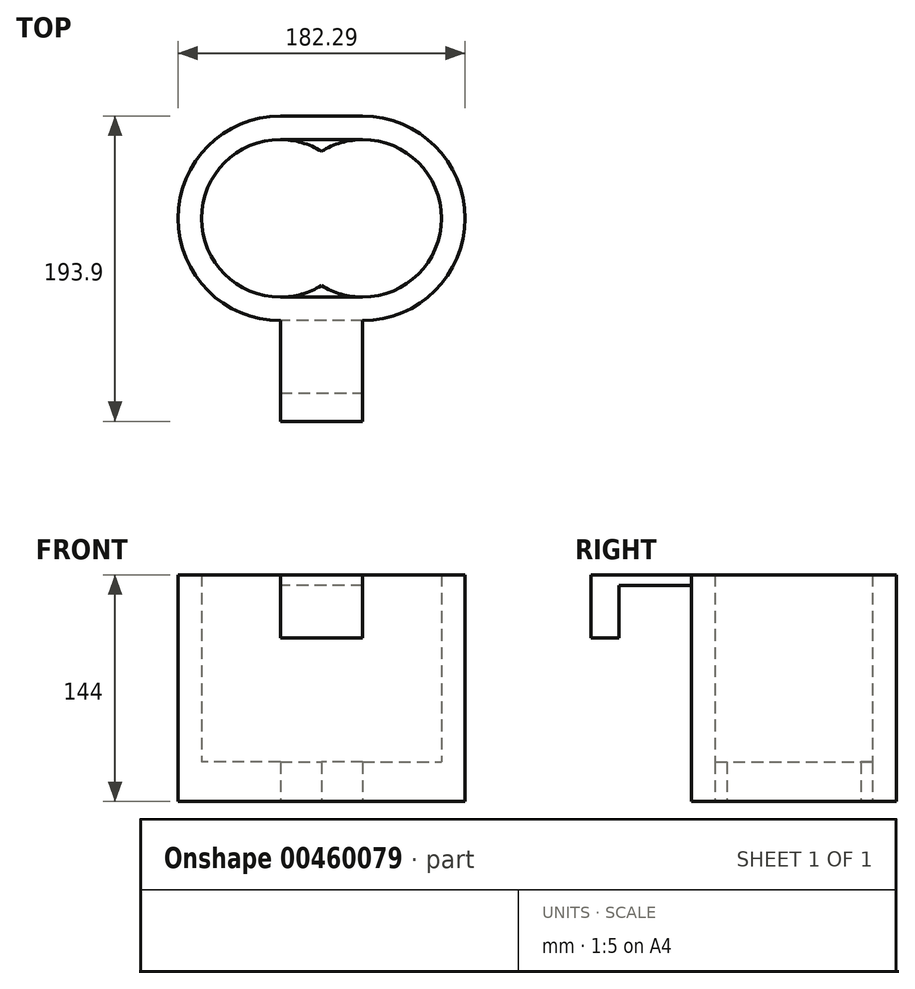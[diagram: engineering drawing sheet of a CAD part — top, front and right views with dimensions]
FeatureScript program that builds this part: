
annotation { "Feature Type Name" : "Feature", "Feature Type Description" : "" }
export const myFeature = defineFeature(function(context is Context, id is Id, definition is map)
    precondition{}
    {
        {
            var Q0;
            Q0=qCreatedBy(makeId("Top.planeOp"),FACE);
            var sketch = newSketch(context, id + "F0", { "sketchPlane" : qUnion([Q0])});
            skCircle(sketch, "E0", {"center": v(-48.66, 0) * mm, "radius": 65 * mm});
            skCircle(sketch, "E1", {"center": v(3.63, 0) * mm, "radius": 65 * mm});
            skLineSegment(sketch, "E2", {"start": v(3.63, -65) * mm, "end": v(-48.66, -65) * mm});
            skLineSegment(sketch, "E3", {"start": v(-48.66, 65) * mm, "end": v(3.63, 65) * mm});
            skCircle(sketch, "E4", {"center": v(-48.66, 0) * mm, "radius": 50 * mm});
            skCircle(sketch, "E5", {"center": v(3.63, 0) * mm, "radius": 50 * mm});
            skLineSegment(sketch, "E6", {"start": v(-48.66, 50) * mm, "end": v(3.63, 50) * mm});
            skLineSegment(sketch, "E7", {"start": v(3.63, -50) * mm, "end": v(-48.66, -50) * mm});
            skSolve(sketch);
        }
        {
            var Q0;
            {var subQ0=sQuery(id+"F0.wireOp",EDGE,"E2");Q0=makeQuery(id+"F0.imprint","IMPRINT",FACE,{"disambiguationData":[TD([[makeQuery(id+"F0.imprint","IMPRINT",EDGE,{"derivedFrom":subQ0}),-1.0]])]});}
            var Q1;
            {var subQ0=sQuery(id+"F0.wireOp",EDGE,"E0");var subQ4=makeQuery(id+"F0.imprint","INTERSECT",VERTEX,{"derivedFrom":[subQ0,sQuery(id+"F0.wireOp",EDGE,"E3")]});Q1=makeQuery(id+"F0.imprint","IMPRINT",FACE,{"disambiguationData":[TD([[makeQuery(id+"F0.imprint","IMPRINT",EDGE,{"disambiguationData":[TD([[subQ4,1.0]])],"derivedFrom":subQ0}),1.0]])]});}
            var Q2;
            {var subQ0=sQuery(id+"F0.wireOp",EDGE,"E3");Q2=makeQuery(id+"F0.imprint","IMPRINT",FACE,{"disambiguationData":[TD([[makeQuery(id+"F0.imprint","IMPRINT",EDGE,{"derivedFrom":subQ0}),-1.0]])]});}
            var Q3;
            {var subQ5=sQuery(id+"F0.wireOp",EDGE,"E1");var subQ7=makeQuery(id+"F0.imprint","INTERSECT",VERTEX,{"derivedFrom":[subQ5,sQuery(id+"F0.wireOp",EDGE,"E3")]});Q3=makeQuery(id+"F0.imprint","IMPRINT",FACE,{"disambiguationData":[TD([[makeQuery(id+"F0.imprint","IMPRINT",EDGE,{"disambiguationData":[TD([[subQ7,-1.0]])],"derivedFrom":subQ5}),1.0]])]});}
            var Q4;
            {var subQ0=sQuery(id+"F0.wireOp",EDGE,"E6");var subQ1=sQuery(id+"F0.wireOp",EDGE,"E0");var subQ2=makeQuery(id+"F0.imprint","INTERSECT",VERTEX,{"derivedFrom":[subQ1,subQ0]});Q4=makeQuery(id+"F0.imprint","IMPRINT",FACE,{"disambiguationData":[TD([[makeQuery(id+"F0.imprint","IMPRINT",EDGE,{"disambiguationData":[TD([[subQ2,-1.0]])],"derivedFrom":subQ1}),1.0]])]});}
            var Q5;
            {var subQ0=sQuery(id+"F0.wireOp",EDGE,"E1");var subQ1=sQuery(id+"F0.wireOp",EDGE,"E0");var subQ2=makeQuery(id+"F0.imprint","INTERSECT",VERTEX,{"disambiguationData":[OD(1.0)],"derivedFrom":[subQ1,subQ0]});Q5=makeQuery(id+"F0.imprint","IMPRINT",FACE,{"disambiguationData":[TD([[makeQuery(id+"F0.imprint","IMPRINT",EDGE,{"disambiguationData":[TD([[subQ2,-1.0]])],"derivedFrom":subQ1}),1.0]])]});}
            extrude(context, id + "F1", {"entities" : qUnion([Q0, Q1, Q2, Q3, Q4, Q5]), "depth" : 144 * mm});
        }
        {
            var Q0;
            Q0=makeQuery(id+"F1.opExtrude","CAP_FACE",FACE,{"disambiguationData":[OSD([sQuery(id+"F0.wireOp",EDGE,"E0"),sQuery(id+"F0.wireOp",EDGE,"E1"),sQuery(id+"F0.wireOp",EDGE,"E2"),sQuery(id+"F0.wireOp",EDGE,"E3"),sQuery(id+"F0.wireOp",EDGE,"E4"),sQuery(id+"F0.wireOp",EDGE,"E5"),sQuery(id+"F0.wireOp",EDGE,"E6"),sQuery(id+"F0.wireOp",EDGE,"E7")])],"isStart":false});
            var sketch = newSketch(context, id + "F2", { "sketchPlane" : qUnion([Q0])});
            skLineSegment(sketch, "E8.bottom", {"start": v(-48.66, -65) * mm, "end": v(3.63, -65) * mm});
            skLineSegment(sketch, "E8.top", {"start": v(-48.66, -111.07) * mm, "end": v(3.63, -111.07) * mm});
            skLineSegment(sketch, "E8.left", {"start": v(-48.66, -65) * mm, "end": v(-48.66, -111.07) * mm});
            skLineSegment(sketch, "E8.right", {"start": v(3.63, -65) * mm, "end": v(3.63, -111.07) * mm});
            skLineSegment(sketch, "E9.top", {"start": v(-48.66, -128.9) * mm, "end": v(3.63, -128.9) * mm});
            skLineSegment(sketch, "E9.left", {"start": v(-48.66, -65) * mm, "end": v(-48.66, -128.9) * mm});
            skLineSegment(sketch, "E9.right", {"start": v(3.63, -65) * mm, "end": v(3.63, -128.9) * mm});
            skSolve(sketch);
        }
        {
            var Q0;
            {var subQ0=sQuery(id+"F2.wireOp",EDGE,"E8.top");Q0=makeQuery(id+"F2.imprint","IMPRINT",FACE,{"disambiguationData":[TD([[makeQuery(id+"F2.imprint","IMPRINT",EDGE,{"derivedFrom":subQ0}),1.0]])]});}
            extrude(context, id + "F3", {"entities" : qUnion([Q0]), "operationType" : NewBodyOperationType.ADD, "oppositeDirection" : true, "depth" : 6.9 * mm});
        }
        {
            var Q0;
            {var subQ0=sQuery(id+"F2.wireOp",EDGE,"E8.top");Q0=makeQuery(id+"F2.imprint","IMPRINT",FACE,{"disambiguationData":[TD([[makeQuery(id+"F2.imprint","IMPRINT",EDGE,{"derivedFrom":subQ0}),-1.0]])]});}
            extrude(context, id + "F4", {"entities" : qUnion([Q0]), "operationType" : NewBodyOperationType.ADD, "oppositeDirection" : true, "depth" : 40.1 * mm});
        }
        {
            var Q0;
            {var subQ0=sQuery(id+"F0.wireOp",EDGE,"E4");var subQ1=sQuery(id+"F0.wireOp",EDGE,"E1");var subQ2=makeQuery(id+"F0.imprint","INTERSECT",VERTEX,{"disambiguationData":[OD(0.0)],"derivedFrom":[subQ1,subQ0]});Q0=makeQuery(id+"F0.imprint","IMPRINT",FACE,{"disambiguationData":[TD([[makeQuery(id+"F0.imprint","IMPRINT",EDGE,{"disambiguationData":[TD([[subQ2,-1.0]])],"derivedFrom":subQ1}),-1.0]])]});}
            var Q1;
            {var subQ0=sQuery(id+"F0.wireOp",EDGE,"E4");var subQ1=sQuery(id+"F0.wireOp",EDGE,"E1");var subQ2=makeQuery(id+"F0.imprint","INTERSECT",VERTEX,{"disambiguationData":[OD(0.0)],"derivedFrom":[subQ1,subQ0]});Q1=makeQuery(id+"F0.imprint","IMPRINT",FACE,{"disambiguationData":[TD([[makeQuery(id+"F0.imprint","IMPRINT",EDGE,{"disambiguationData":[TD([[subQ2,-1.0]])],"derivedFrom":subQ1}),1.0]])]});}
            var Q2;
            {var subQ0=sQuery(id+"F0.wireOp",EDGE,"E5");var subQ1=sQuery(id+"F0.wireOp",EDGE,"E4");var subQ2=makeQuery(id+"F0.imprint","INTERSECT",VERTEX,{"disambiguationData":[OD(0.0)],"derivedFrom":[subQ1,subQ0]});Q2=makeQuery(id+"F0.imprint","IMPRINT",FACE,{"disambiguationData":[TD([[makeQuery(id+"F0.imprint","IMPRINT",EDGE,{"disambiguationData":[TD([[subQ2,1.0]])],"derivedFrom":subQ1}),1.0]])]});}
            var Q3;
            {var subQ0=sQuery(id+"F0.wireOp",EDGE,"E5");var subQ1=sQuery(id+"F0.wireOp",EDGE,"E0");var subQ2=makeQuery(id+"F0.imprint","INTERSECT",VERTEX,{"disambiguationData":[OD(0.0)],"derivedFrom":[subQ1,subQ0]});Q3=makeQuery(id+"F0.imprint","IMPRINT",FACE,{"disambiguationData":[TD([[makeQuery(id+"F0.imprint","IMPRINT",EDGE,{"disambiguationData":[TD([[subQ2,1.0]])],"derivedFrom":subQ1}),1.0]])]});}
            var Q4;
            {var subQ0=sQuery(id+"F0.wireOp",EDGE,"E5");var subQ1=sQuery(id+"F0.wireOp",EDGE,"E0");var subQ2=makeQuery(id+"F0.imprint","INTERSECT",VERTEX,{"disambiguationData":[OD(0.0)],"derivedFrom":[subQ1,subQ0]});Q4=makeQuery(id+"F0.imprint","IMPRINT",FACE,{"disambiguationData":[TD([[makeQuery(id+"F0.imprint","IMPRINT",EDGE,{"disambiguationData":[TD([[subQ2,1.0]])],"derivedFrom":subQ1}),-1.0]])]});}
            extrude(context, id + "F5", {"entities" : qUnion([Q0, Q1, Q2, Q3, Q4]), "operationType" : NewBodyOperationType.ADD, "depth" : 25 * mm});
        }
    });
